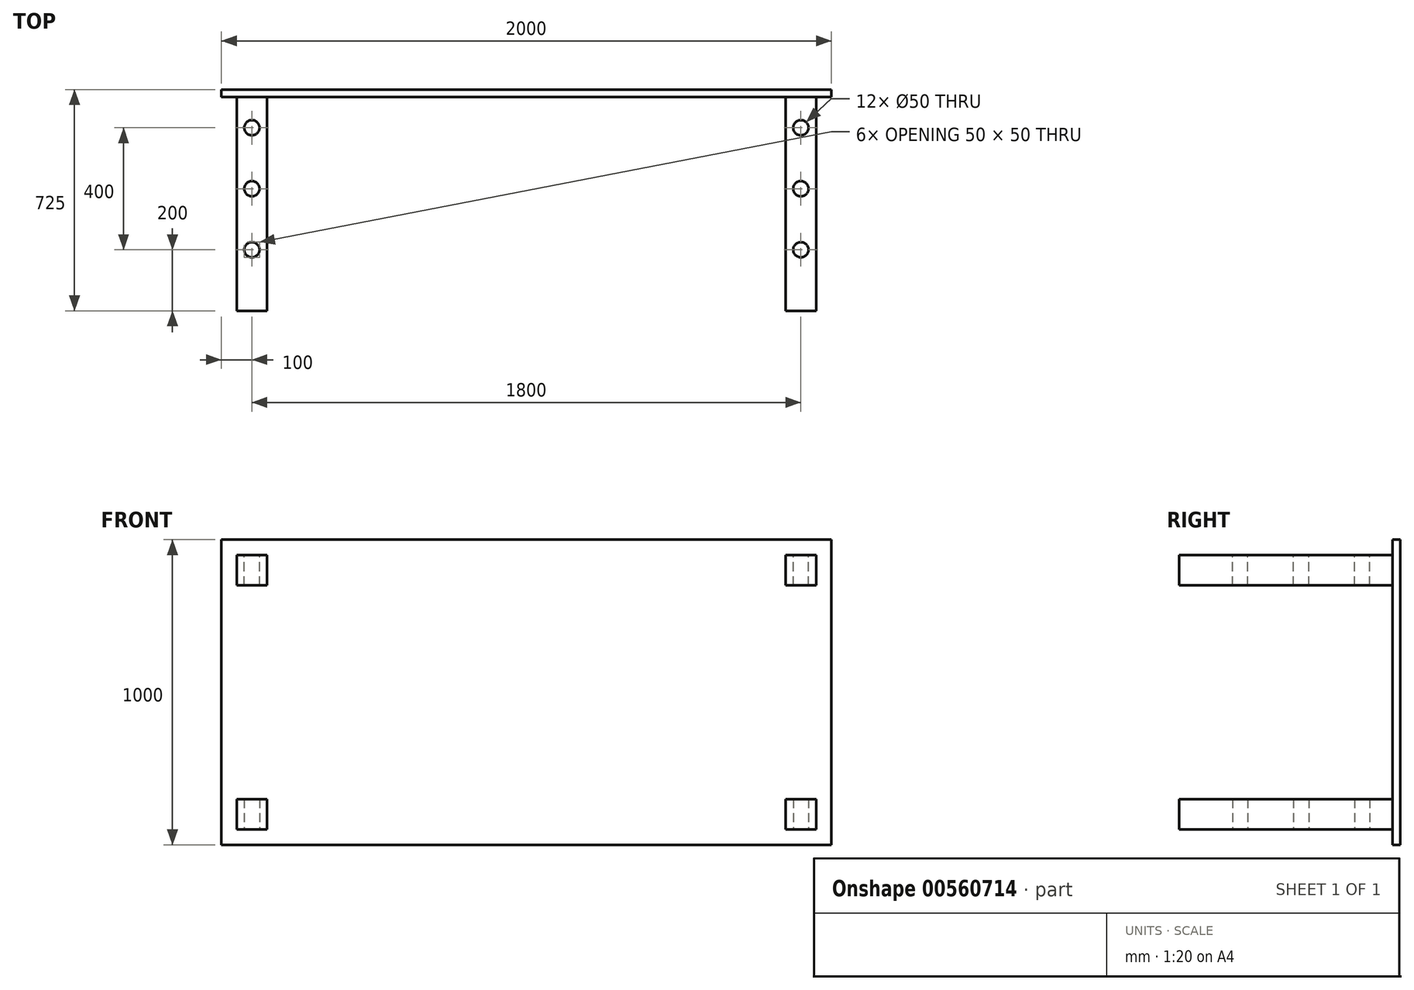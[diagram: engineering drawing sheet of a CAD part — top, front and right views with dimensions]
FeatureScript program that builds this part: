
annotation { "Feature Type Name" : "Feature", "Feature Type Description" : "" }
export const myFeature = defineFeature(function(context is Context, id is Id, definition is map)
    precondition{}
    {
        {
            var Q0;
            Q0=qCreatedBy(makeId("Front.planeOp"),FACE);
            var sketch = newSketch(context, id + "F0", { "sketchPlane" : qUnion([Q0])});
            skLineSegment(sketch, "E0.bottom", {"start": v(0, 0) * mm, "end": v(1000, 0) * mm});
            skLineSegment(sketch, "E0.top", {"start": v(0, 500) * mm, "end": v(1000, 500) * mm});
            skLineSegment(sketch, "E0.left", {"start": v(0, 0) * mm, "end": v(0, 500) * mm});
            skLineSegment(sketch, "E0.right", {"start": v(1000, 0) * mm, "end": v(1000, 500) * mm});
            skSolve(sketch);
        }
        {
            var Q0;
            Q0=qCreatedBy(makeId("Front.planeOp"),FACE);
            var sketch = newSketch(context, id + "F1", { "sketchPlane" : qUnion([Q0])});
            skLineSegment(sketch, "E1.bottom", {"start": v(50, 150) * mm, "end": v(150, 150) * mm});
            skLineSegment(sketch, "E1.top", {"start": v(50, 50) * mm, "end": v(150, 50) * mm});
            skLineSegment(sketch, "E1.left", {"start": v(50, 150) * mm, "end": v(50, 50) * mm});
            skLineSegment(sketch, "E1.right", {"start": v(150, 150) * mm, "end": v(150, 50) * mm});
            skSolve(sketch);
        }
        {
            var Q0;
            Q0=makeQuery(id+"F0.imprint","IMPRINT",FACE,{"disambiguationData":[TD([[makeQuery(id+"F0.imprint","IMPRINT",EDGE,{"derivedFrom":sQuery(id+"F0.wireOp",EDGE,"E0.bottom")}),1.0]])]});
            extrude(context, id + "F2", {"entities" : qUnion([Q0]), "depth" : 25 * mm, "offsetDistance" : 25 * mm});
        }
        {
            var Q0;
            Q0 = qSketchRegion(id + "F1", true);
            extrude(context, id + "F3", {"entities" : qUnion([Q0]), "operationType" : NewBodyOperationType.ADD, "depth" : 725 * mm, "offsetDistance" : 25 * mm});
        }
        {
            var Q0;
            Q0=makeQuery(id+"F3.opExtrude","SWEPT_FACE",FACE,{"disambiguationData":[OSD([sQuery(id+"F1.wireOp",EDGE,"E1.top")])]});
            var sketch = newSketch(context, id + "F4", { "sketchPlane" : qUnion([Q0])});
            skCircle(sketch, "E2", {"center": v(100, 125) * mm, "radius": 25 * mm});
            skCircle(sketch, "E3", {"center": v(100, 325) * mm, "radius": 25 * mm});
            skCircle(sketch, "E4", {"center": v(100, 525) * mm, "radius": 25 * mm});
            skSolve(sketch);
        }
        {
            var Q0;
            Q0 = qSketchRegion(id + "F4", true);
            extrude(context, id + "F5", {"entities" : qUnion([Q0]), "operationType" : NewBodyOperationType.REMOVE, "endBound" : BoundingType.UP_TO_NEXT, "oppositeDirection" : true, "depth" : 25 * mm, "offsetDistance" : 25 * mm});
        }
        {
            var Q0;
            Q0=makeQuery(id+"F2.opExtrude","SWEPT_FACE",FACE,{"disambiguationData":[OSD([sQuery(id+"F0.wireOp",EDGE,"E0.right")])]});
            cPlane(context, id + "F6", {"entities" : qUnion([Q0]), "cplaneType" : CPlaneType.OFFSET, "offset" : 0 * mm, "width" : 150 * mm, "height" : 150 * mm});
        }
        {
            var Q0;
            Q0=makeQuery(id+"F2.opExtrude","SWEPT_FACE",FACE,{"disambiguationData":[OSD([sQuery(id+"F0.wireOp",EDGE,"E0.top")])]});
            cPlane(context, id + "F7", {"entities" : qUnion([Q0]), "cplaneType" : CPlaneType.OFFSET, "offset" : 0 * mm, "width" : 150 * mm, "height" : 150 * mm});
        }
        {
            var Q0;
            Q0=makeQuery(id+"F2.opExtrude","SWEPT_BODY",BODY,{"disambiguationData":[OSD([sQuery(id+"F0.wireOp",EDGE,"E0.bottom"),sQuery(id+"F0.wireOp",EDGE,"E0.top"),sQuery(id+"F0.wireOp",EDGE,"E0.left"),sQuery(id+"F0.wireOp",EDGE,"E0.right")])]});
            var Q1;
            Q1=qCreatedBy(id+"F7.planeOp",FACE);
            mirror(context, id + "F8", {"operationType" : NewBodyOperationType.ADD, "entities" : qUnion([Q0]), "mirrorPlane" : qUnion([Q1])});
        }
        {
            var Q0;
            Q0=makeQuery(id+"F2.opExtrude","SWEPT_BODY",BODY,{"disambiguationData":[OSD([sQuery(id+"F0.wireOp",EDGE,"E0.bottom"),sQuery(id+"F0.wireOp",EDGE,"E0.top"),sQuery(id+"F0.wireOp",EDGE,"E0.left"),sQuery(id+"F0.wireOp",EDGE,"E0.right")])]});
            var Q1;
            Q1=qCreatedBy(id+"F6.planeOp",FACE);
            mirror(context, id + "F9", {"operationType" : NewBodyOperationType.ADD, "entities" : qUnion([Q0]), "mirrorPlane" : qUnion([Q1])});
        }
    });
